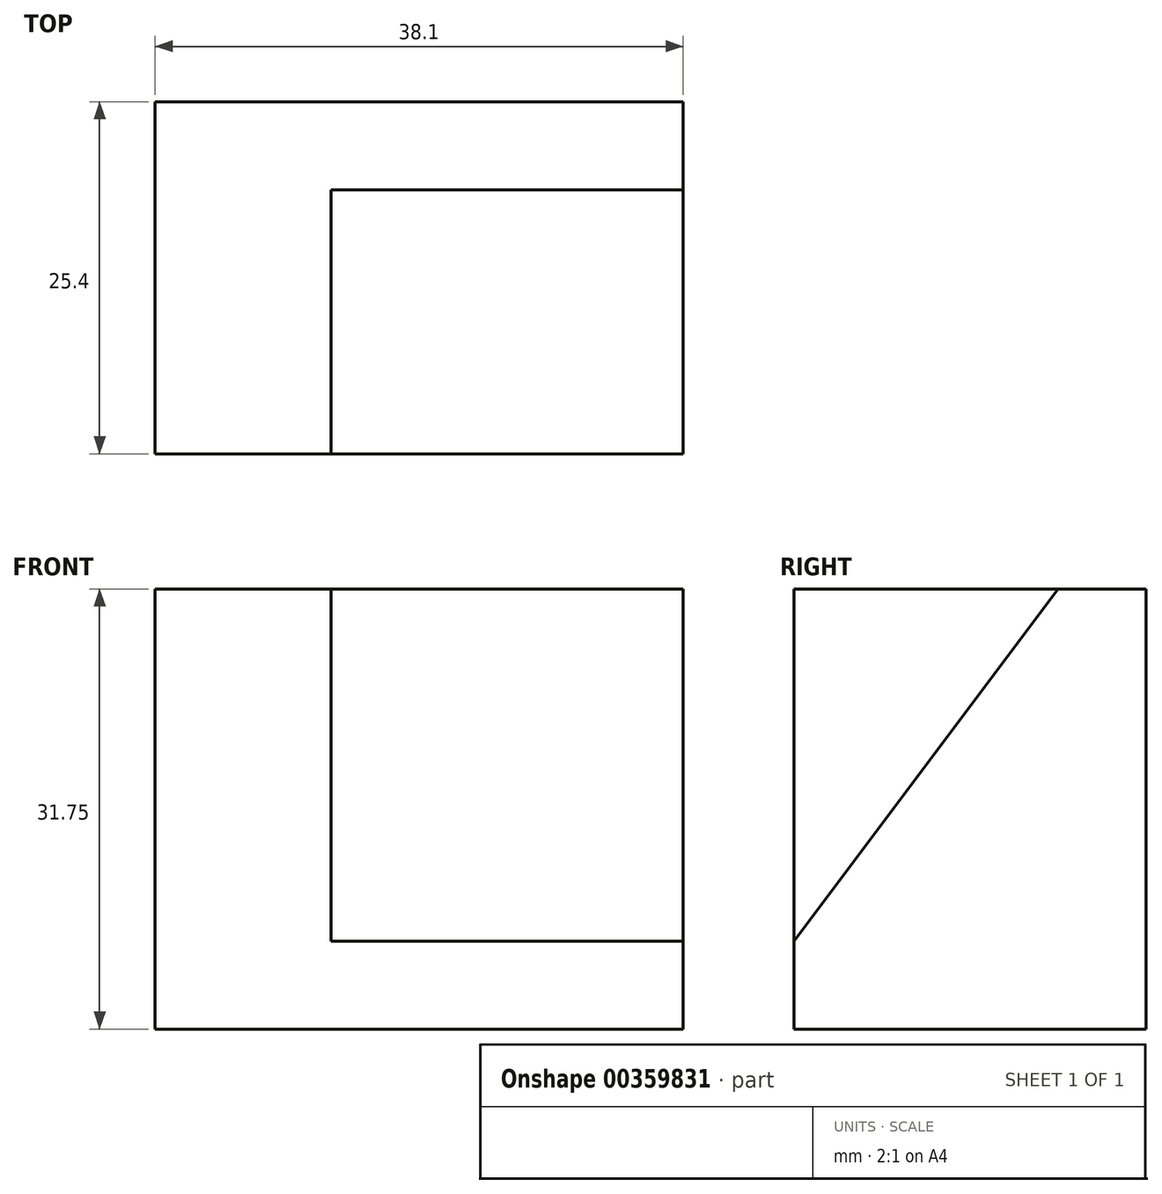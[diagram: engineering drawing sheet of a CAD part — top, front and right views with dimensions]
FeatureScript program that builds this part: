
annotation { "Feature Type Name" : "Feature", "Feature Type Description" : "" }
export const myFeature = defineFeature(function(context is Context, id is Id, definition is map)
    precondition{}
    {
        {
            var Q0;
            Q0=qCreatedBy(makeId("Front.planeOp"),FACE);
            var sketch = newSketch(context, id + "F0", { "sketchPlane" : qUnion([Q0])});
            skLineSegment(sketch, "E0", {"start": v(0, 0) * mm, "end": v(-38.1, 0) * mm});
            skLineSegment(sketch, "E1", {"start": v(-38.1, 0) * mm, "end": v(-38.1, 31.75) * mm});
            skLineSegment(sketch, "E2", {"start": v(-38.1, 31.75) * mm, "end": v(0, 31.75) * mm});
            skLineSegment(sketch, "E3", {"start": v(0, 31.75) * mm, "end": v(0, 0) * mm});
            skSolve(sketch);
        }
        {
            var Q0;
            Q0=makeQuery(id+"F0.imprint","IMPRINT",FACE,{"disambiguationData":[TD([[makeQuery(id+"F0.imprint","IMPRINT",EDGE,{"derivedFrom":sQuery(id+"F0.wireOp",EDGE,"E0")}),-1.0]])]});
            extrude(context, id + "F1", {"entities" : qUnion([Q0]), "depth" : 25.4 * mm});
        }
        {
            var Q0;
            Q0=makeQuery(id+"F1.opExtrude","SWEPT_FACE",FACE,{"disambiguationData":[OSD([sQuery(id+"F0.wireOp",EDGE,"E3")])]});
            var sketch = newSketch(context, id + "F2", { "sketchPlane" : qUnion([Q0])});
            skLineSegment(sketch, "E4", {"start": v(-25.4, 6.35) * mm, "end": v(-25.4, 31.75) * mm});
            skLineSegment(sketch, "E5", {"start": v(-25.4, 31.75) * mm, "end": v(-6.35, 31.75) * mm});
            skLineSegment(sketch, "E6", {"start": v(-6.35, 31.75) * mm, "end": v(-25.4, 6.35) * mm});
            skSolve(sketch);
        }
        {
            var Q0;
            Q0 = qSketchRegion(id + "F2", true);
            extrude(context, id + "F3", {"entities" : qUnion([Q0]), "operationType" : NewBodyOperationType.REMOVE, "oppositeDirection" : true, "depth" : 25.4 * mm});
        }
    });
